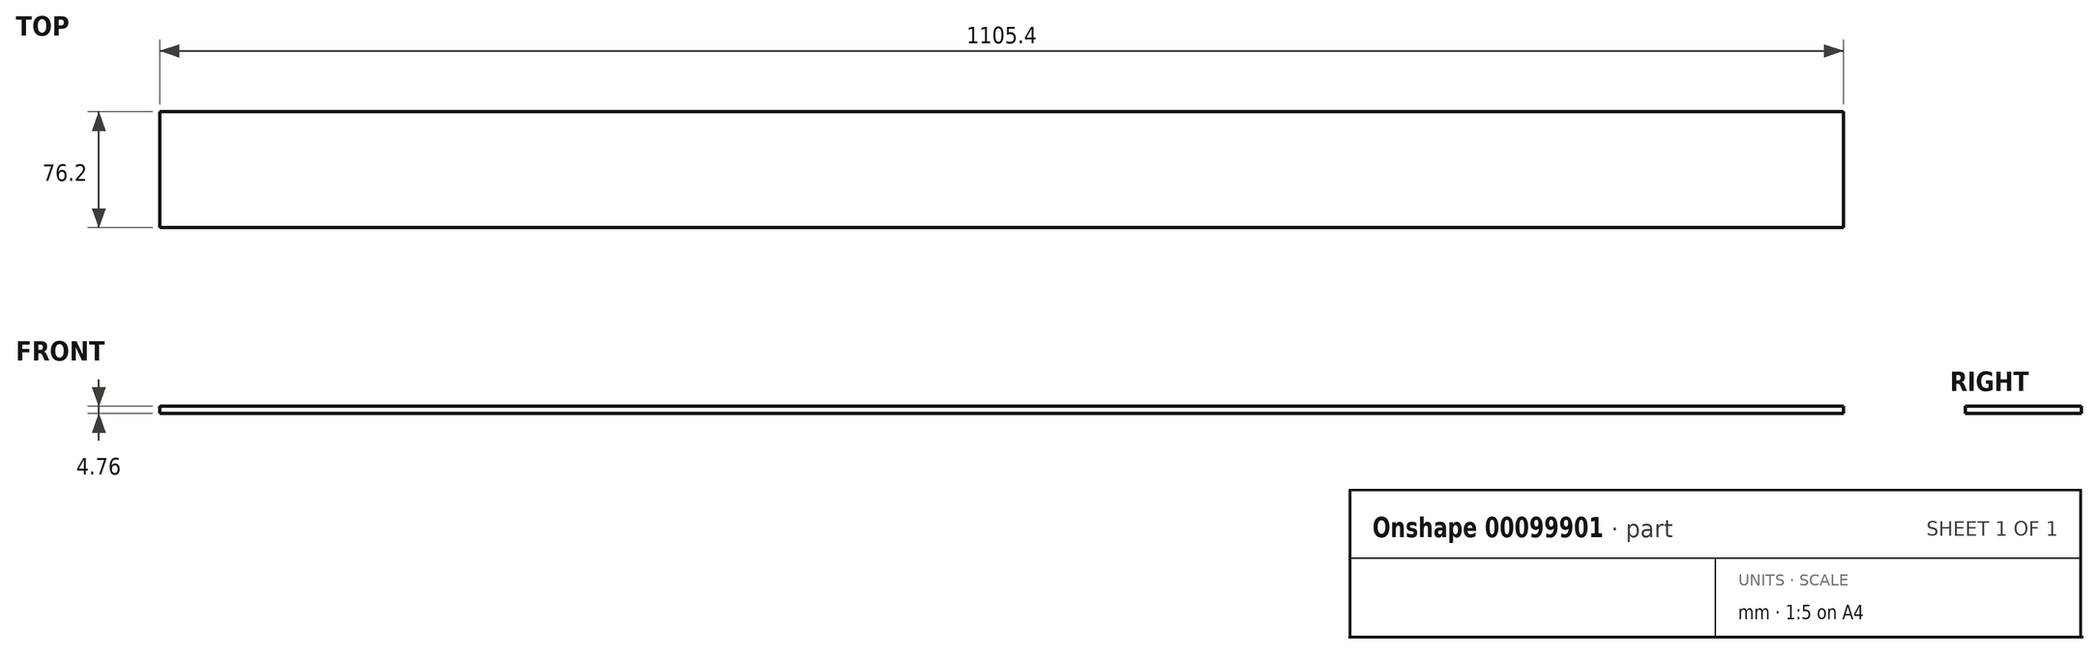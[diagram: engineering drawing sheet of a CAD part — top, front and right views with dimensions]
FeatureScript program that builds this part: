
annotation { "Feature Type Name" : "Feature", "Feature Type Description" : "" }
export const myFeature = defineFeature(function(context is Context, id is Id, definition is map)
    precondition{}
    {
        {
            var Q0;
            Q0=qCreatedBy(makeId("Top.planeOp"),FACE);
            var sketch = newSketch(context, id + "F0", { "sketchPlane" : qUnion([Q0])});
            skLineSegment(sketch, "E0.bottom", {"start": v(552.7, 38.1) * mm, "end": v(-552.7, 38.1) * mm});
            skLineSegment(sketch, "E0.top", {"start": v(552.7, -38.1) * mm, "end": v(-552.7, -38.1) * mm});
            skLineSegment(sketch, "E0.left", {"start": v(552.7, 38.1) * mm, "end": v(552.7, -38.1) * mm});
            skLineSegment(sketch, "E0.right", {"start": v(-552.7, 38.1) * mm, "end": v(-552.7, -38.1) * mm});
            skPoint(sketch, "E0.middle", {"position": v(0, 0) * mm});
            skSolve(sketch);
        }
        {
            var Q0;
            Q0 = qSketchRegion(id + "F0", true);
            extrude(context, id + "F1", {"entities" : qUnion([Q0]), "depth" : 4.76 * mm});
        }
    });
